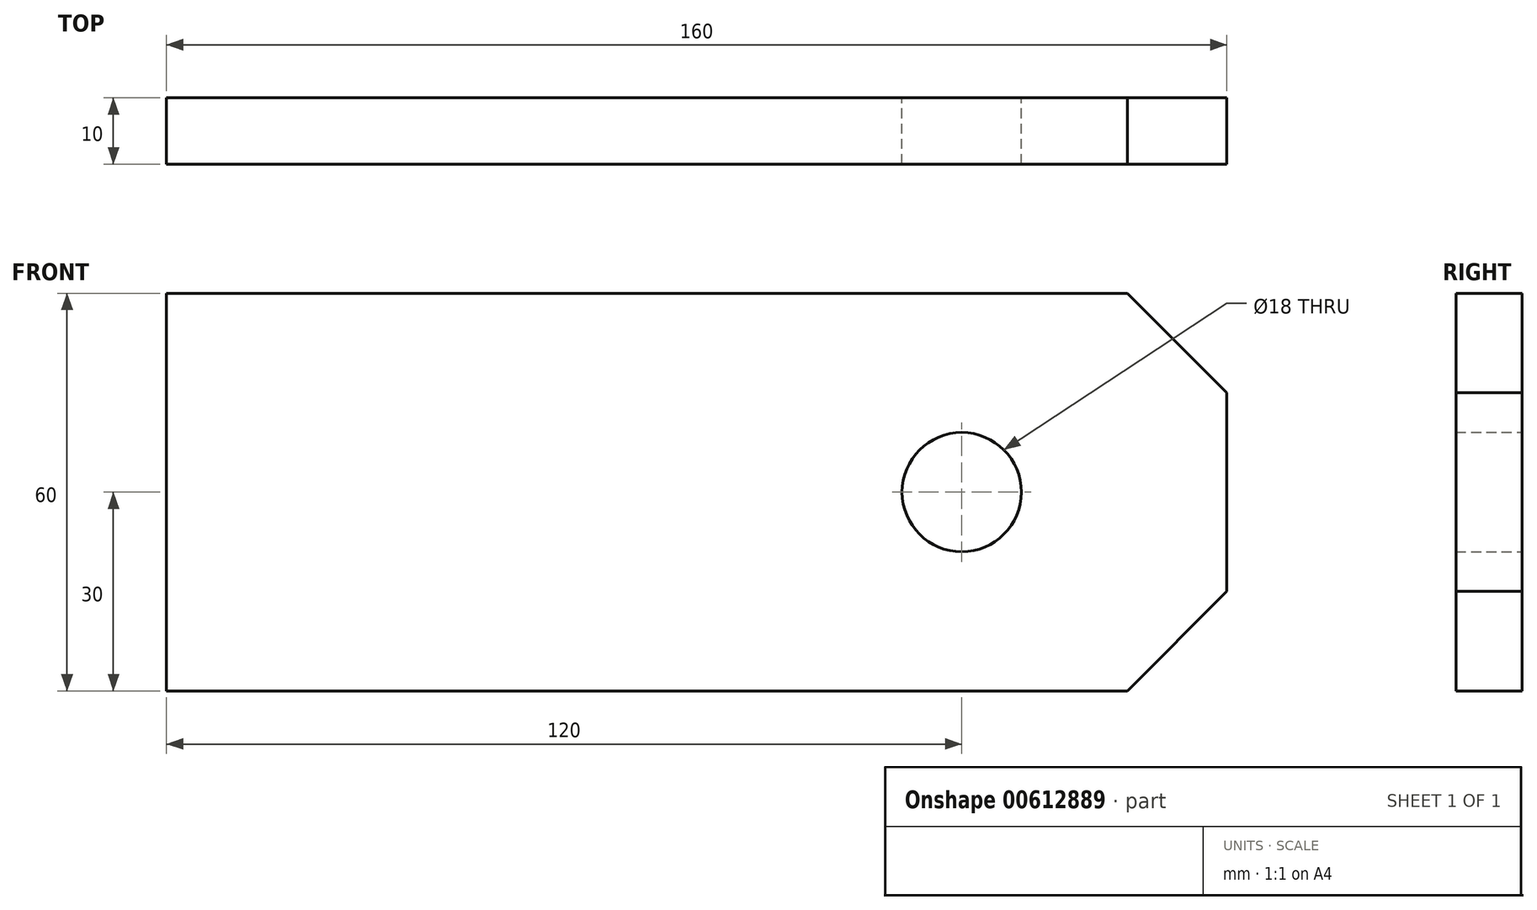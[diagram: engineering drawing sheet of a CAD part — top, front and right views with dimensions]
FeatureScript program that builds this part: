
annotation { "Feature Type Name" : "Feature", "Feature Type Description" : "" }
export const myFeature = defineFeature(function(context is Context, id is Id, definition is map)
    precondition{}
    {
        {
            var Q0;
            Q0=qCreatedBy(makeId("Front.planeOp"),FACE);
            var sketch = newSketch(context, id + "F0", { "sketchPlane" : qUnion([Q0])});
            skLineSegment(sketch, "E0.bottom", {"start": v(80, 30) * mm, "end": v(-80, 30) * mm});
            skLineSegment(sketch, "E0.top", {"start": v(80, -30) * mm, "end": v(-80, -30) * mm});
            skLineSegment(sketch, "E0.left", {"start": v(80, 30) * mm, "end": v(80, -30) * mm});
            skLineSegment(sketch, "E0.right", {"start": v(-80, 30) * mm, "end": v(-80, -30) * mm});
            skPoint(sketch, "E0.middle", {"position": v(0, 0) * mm});
            skCircle(sketch, "E1", {"center": v(40, 0) * mm, "radius": 9 * mm});
            skSolve(sketch);
        }
        {
            var Q0;
            Q0=makeQuery(id+"F0.imprint","IMPRINT",FACE,{"disambiguationData":[TD([[makeQuery(id+"F0.imprint","IMPRINT",EDGE,{"derivedFrom":sQuery(id+"F0.wireOp",EDGE,"E0.bottom")}),1.0]])]});
            extrude(context, id + "F1", {"entities" : qUnion([Q0]), "endBound" : BoundingType.SYMMETRIC, "depth" : 10 * mm, "offsetDistance" : 25 * mm});
        }
        {
            var Q0;
            Q0=makeQuery(id+"F1.opExtrude","SWEPT_EDGE",EDGE,{"disambiguationData":[OSD([sQuery(id+"F0.wireOp",EDGE,"E0.bottom"),sQuery(id+"F0.wireOp",EDGE,"E0.left")])]});
            var Q1;
            Q1=makeQuery(id+"F1.opExtrude","SWEPT_EDGE",EDGE,{"disambiguationData":[OSD([sQuery(id+"F0.wireOp",EDGE,"E0.top"),sQuery(id+"F0.wireOp",EDGE,"E0.left")])]});
            chamfer(context, id + "F2", {"entities" : qUnion([Q0, Q1]), "width" : 15 * mm, "tangentPropagation" : true});
        }
    });
